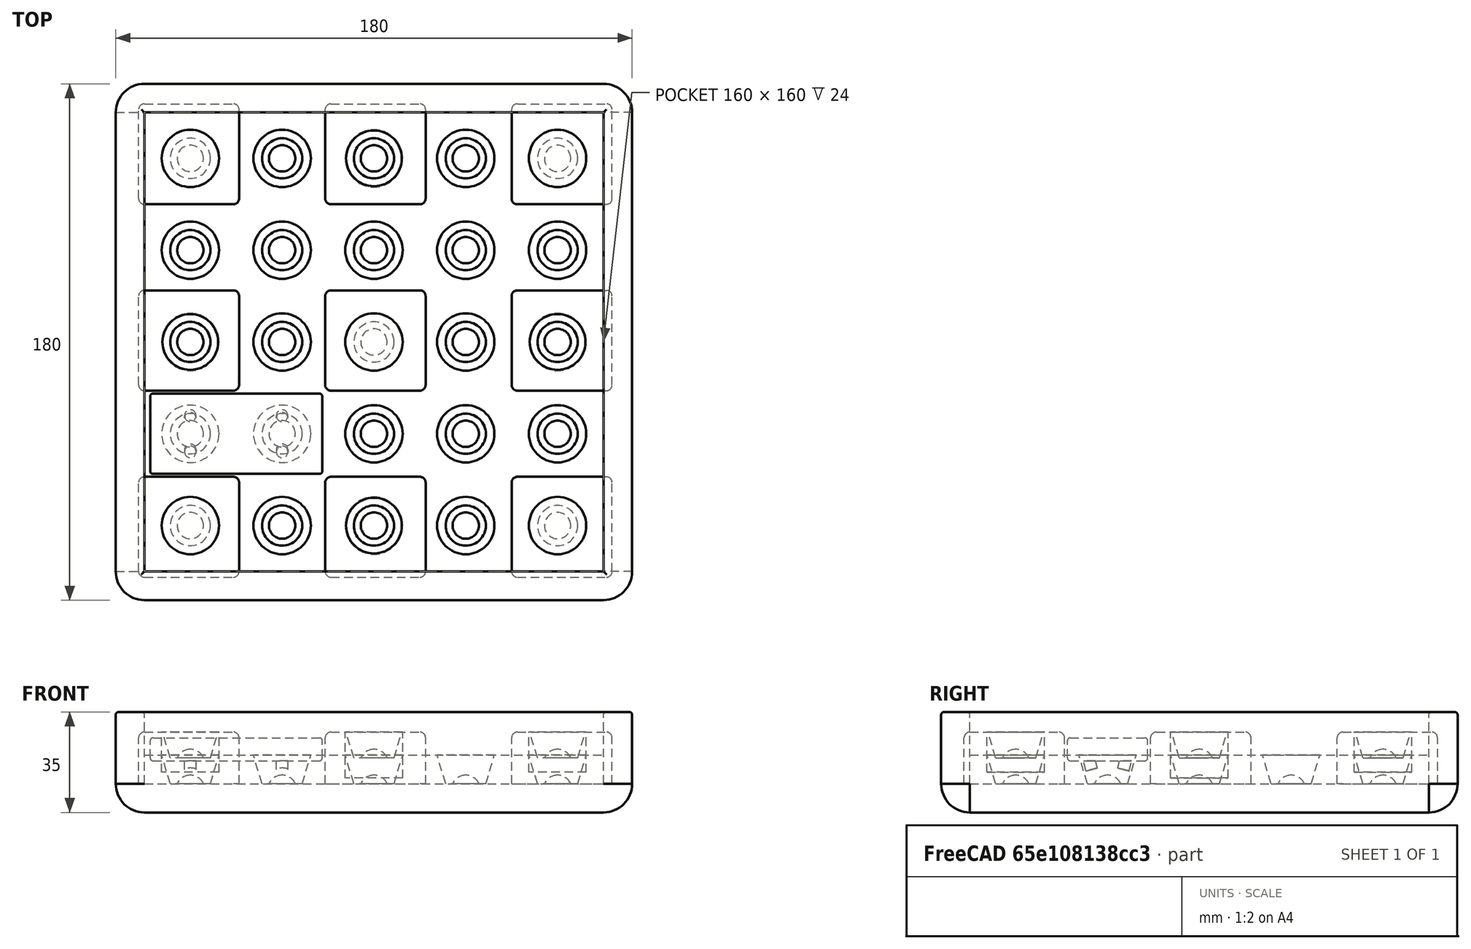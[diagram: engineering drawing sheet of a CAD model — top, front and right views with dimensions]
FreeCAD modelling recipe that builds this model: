
FCSTD DOCUMENT  (FreeCAD 0.16R6712 (Git))
Label: diseño tablero 2
License: All rights reserved
LicenseURL: http://en.wikipedia.org/wiki/All_rights_reserved
objects: Part::Cylinder×8, Part::FeaturePython×5, Part::Cut×5, Part::Box×4, Part::Fillet×3, Part::Fuse×3, Part::Cone×2, Part::Sphere×2, Part::Thickness×1, App::DocumentObjectGroup×1, Part::MultiFuse×1
note: 34 computed .brp shape members not serialized (recipe doc carries the construction recipe); baked Part::Feature solids carry a one-line shape summary decoded from their .brp

FEATURE [Part::Box] Box  label="Cube"
  Height = 25
  Length = 160
  Width = 160
FEATURE [Part::Thickness] Thickness  label="Borde"
  Faces = -> Box [Face6]
  Intersection = false
  Join = 0
  Mode = 0
  SelfIntersection = false
  Value = 10
FEATURE [Part::Box] Box001  label="Base"
  Height = 10
  Length = 160
  Width = 160
FEATURE [Part::Box] Box002  label="saliente"
  Height = 18
  Length = 35
  Width = 35
FEATURE [Part::Fillet] Fillet001  label="SalienteSuavizado"
  Base = -> Box002
  Edges = 8 edges r=2: [Edge1,Edge2,Edge3,Edge5,Edge6,Edge7,Edge10,Edge12]
  Placement = pos=(-2,-2,0) rot=(0,0,1;0rad)
FEATURE [Part::FeaturePython] Array  label="Salientes"  # Draft array (typed FeaturePython)
  Angle = 360
  ArrayType = 0
  Axis = (0,0,1)
  Base = -> Fillet001
  Center = (0,0,0)
  Fuse = false
  IntervalAxis = (0,0,0)
  IntervalX = (65,0,0)
  IntervalY = (0,65,0)
  IntervalZ = (0,0,0)
  NumberPolar = 1
  NumberX = 3
  NumberY = 3
  NumberZ = 1
FEATURE [Part::Fillet] Fillet  label="BordeexteriorSuavizado"
  Base = -> Thickness
  Edges = 8 edges r=1: [Edge2,Edge6,Edge8,Edge12,Edge13,Edge15,Edge17,Edge19]
FEATURE [Part::Cone] Cone
  Angle = 360
  Height = 10
  Placement = pos=(0,0,38) rot=(0,0,1;0rad)
  Radius1 = 7
  Radius2 = 10
FEATURE [Part::Sphere] Sphere
  Angle1 = -90
  Angle2 = 90
  Angle3 = 360
  Placement = pos=(0,0,36) rot=(0,0,1;0rad)
  Radius = 5
FEATURE [Part::Cut] Cut  label="AgujeroAlto"
  Base = -> Cone
  Placement = pos=(16,16,-29) rot=(0,0,1;0rad)
  Tool = -> Sphere
FEATURE [Part::Cone] Cone001
  Angle = 360
  Height = 10
  Placement = pos=(0,0,38) rot=(0,0,1;0rad)
  Radius1 = 7
  Radius2 = 10
FEATURE [Part::Sphere] Sphere001
  Angle1 = -90
  Angle2 = 90
  Angle3 = 360
  Placement = pos=(0,0,36) rot=(0,0,1;0rad)
  Radius = 5
FEATURE [Part::Cut] Cut001  label="AgujeroBajo"
  Base = -> Cone001
  Placement = pos=(16,16,-38) rot=(0,0,1;0rad)
  Tool = -> Sphere001
FEATURE [Part::FeaturePython] Array001  label="AgujerosAltos"  # Draft array (typed FeaturePython)
  Angle = 360
  ArrayType = 0
  Axis = (0,0,1)
  Base = -> Cut
  Center = (0,0,0)
  Fuse = false
  IntervalAxis = (0,0,0)
  IntervalX = (64,0,0)
  IntervalY = (0,64,0)
  IntervalZ = (0,0,0)
  NumberPolar = 1
  NumberX = 3
  NumberY = 3
  NumberZ = 1
FEATURE [Part::FeaturePython] Array002  label="AgujerosBajos"  # Draft array (typed FeaturePython)
  Angle = 360
  ArrayType = 0
  Axis = (0,0,1)
  Base = -> Cut001
  Center = (0,0,0)
  Fuse = false
  IntervalAxis = (0,0,0)
  IntervalX = (32,0,0)
  IntervalY = (0,32,0)
  IntervalZ = (0,0,0)
  NumberPolar = 1
  NumberX = 5
  NumberY = 5
  NumberZ = 1
FEATURE [Part::Cut] Cut002  label="BaseConAgujeros"
  Base = -> Box001
  Tool = -> Array002
FEATURE [Part::Cut] Cut003  label="SalientesConAgujeros"
  Base = -> Array
  Tool = -> Array001
FEATURE [Part::Cylinder] Cylinder  label="Madriguera"
  Angle = 360
  Height = 15
  Placement = pos=(16,16,4) rot=(0,0,1;0rad)
  Radius = 10
FEATURE [Part::FeaturePython] Array003  label="Madrigueras"  # Draft array (typed FeaturePython)
  Angle = 360
  ArrayType = 0
  Axis = (0,0,1)
  Base = -> Cylinder
  Center = (0,0,0)
  Fuse = false
  IntervalAxis = (0,0,0)
  IntervalX = (128,0,0)
  IntervalY = (0,128,0)
  IntervalZ = (0,0,0)
  NumberPolar = 1
  NumberX = 2
  NumberY = 2
  NumberZ = 1
FEATURE [Part::Cylinder] Cylinder001  label="MadrigueraCentro"
  Angle = 360
  Height = 20
  Placement = pos=(80,80,2) rot=(0,0,1;0rad)
  Radius = 10
FEATURE [Part::Cylinder] Cylinder002  label="RellenaMadriguera001"
  Angle = 360
  Height = 18
  Placement = pos=(16,16,0) rot=(0,0,1;0rad)
  Radius = 10
FEATURE [Part::FeaturePython] Array004  label="RellenaMadriguera"  # Draft array (typed FeaturePython)
  Angle = 360
  ArrayType = 0
  Axis = (0,0,1)
  Base = -> Cylinder002
  Center = (0,0,0)
  Fuse = false
  IntervalAxis = (0,0,0)
  IntervalX = (128,0,0)
  IntervalY = (0,128,0)
  IntervalZ = (0,0,0)
  NumberPolar = 1
  NumberX = 2
  NumberY = 2
  NumberZ = 1
FEATURE [Part::Cylinder] Cylinder003  label="RellenaMadrigueraCentro"
  Angle = 360
  Height = 18
  Placement = pos=(80,80,0) rot=(0,0,1;0rad)
  Radius = 10
FEATURE [Part::Fuse] Fusion001  label="RellenaMadrigueras"
  Base = -> Array004
  Tool = -> Cylinder003
FEATURE [Part::Fuse] Fusion002  label="SalientesSinAgujerosIndeseados"
  Base = -> Cut003
  Tool = -> Fusion001
FEATURE [Part::Fuse] Fusion  label="MadriguerasTodas"
  Base = -> Array003
  Tool = -> Cylinder001
FEATURE [Part::Cut] Cut004  label="SalientesArreglados"
  Base = -> Fusion002
  Tool = -> Fusion
FEATURE [Part::Box] Box003  label="baseZoro"
  Height = 8
  Length = 60
  Placement = pos=(0,0,29) rot=(0,0,1;0rad)
  Width = 28
FEATURE [Part::Fillet] Fillet002  label="baseZorroRedondeada"
  Base = -> Box003
  Edges = 12 edges r=1: [Edge1,Edge2,Edge3,Edge4,Edge5,Edge6,Edge7,Edge8,Edge9,Edge10,Edge11,Edge12]
  Placement = pos=(2,34,-21) rot=(0,0,1;0rad)
FEATURE [Part::Cylinder] Cylinder004  label="Cylinder"
  Angle = 360
  Height = 5
  Placement = pos=(48,53.5,5) rot=(-1,0,0;0.261799rad)
  Radius = 2
FEATURE [Part::Cylinder] Cylinder005  label="Cylinder001"
  Angle = 360
  Height = 5
  Placement = pos=(16,42.5,5) rot=(1,0,0;0.261799rad)
  Radius = 2
FEATURE [Part::Cylinder] Cylinder006  label="Cylinder008"
  Angle = 360
  Height = 5
  Placement = pos=(16,53.5,5) rot=(-1,0,0;0.261799rad)
  Radius = 2
FEATURE [Part::Cylinder] Cylinder007  label="Cylinder009"
  Angle = 360
  Height = 5
  Placement = pos=(48,42.5,5) rot=(1,0,0;0.261799rad)
  Radius = 2
FEATURE [App::DocumentObjectGroup] Group  label="sujeccionBaseZorro"
FEATURE [Part::MultiFuse] Fusion003  label="BaseZorroCompleta"
  Shapes = -> [Cylinder005,Cylinder007,Cylinder004,Cylinder006,Fillet002]
